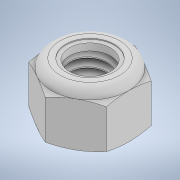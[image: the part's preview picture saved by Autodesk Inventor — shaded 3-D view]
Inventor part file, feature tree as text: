
AUTODESK INVENTOR PART (.ipt)
format: ipt  version: 2021 (Build 250183000, 183)  size: 364,544 bytes
history: native  units: in
note: dims shown in document units (in); Inventor stores cm internally (conversion verified against a paired STEP export)
features: revolve x1, boolean_combine x1
ambient origin geometry x8: Origin, YZ Plane, XZ Plane, XY Plane, X Axis, Y Axis, Z Axis, Center Point
bodies: Solid1 (feature_tree), Solid2 (feature_tree)
feature tree (2):
  revolve  "Revolve2"  [1 undecoded]
  boolean_combine  "Combine1"
note: 1 required parameter value undecoded (feature->parameter linkage not recoverable at this tier; creation-order binding heuristic only, values carry confidence <= 0.55)
